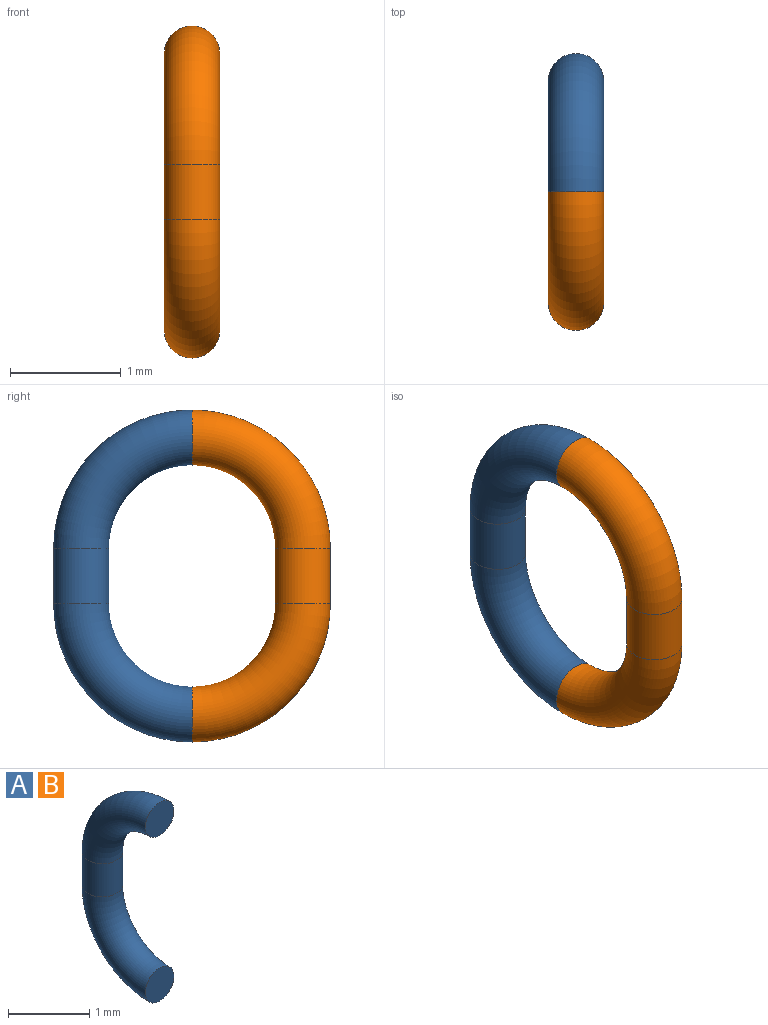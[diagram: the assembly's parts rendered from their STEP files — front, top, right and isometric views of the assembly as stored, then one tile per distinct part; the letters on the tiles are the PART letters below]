
ASSEMBLY  parts=2 mates=1
PART A: 5 faces, bbox 0.5x1.4x3.2 mm
  f0: plane 0.5x0.5mm, normal (0,-1,0), area 0.2mm2, adj f2
  f1: plane 0.5x0.5mm, normal (0,-1,0), area 0.2mm2, adj f4
  f2: torus R=1mm, axis (1,0,0), area 2.5mm2, adj f0,f3
  f3: cylinder r=0.25mm len=0.5mm, axis (0,0,1), area 0.8mm2, adj f2,f4
  f4: torus R=1mm, axis (1,0,0), area 2.5mm2, adj f1,f3
PART B: same geometry as A
PLACE A t=(-5.28,-26.95,-8.06)mm
PLACE B rot(axis=(0,0,1),180deg) t=(-5.28,-26.95,-8.06)mm
MATE fastened B.f1 <-> A.f1  axis (0,1,0) through (-5.28,-26.95,-5.56)mm
